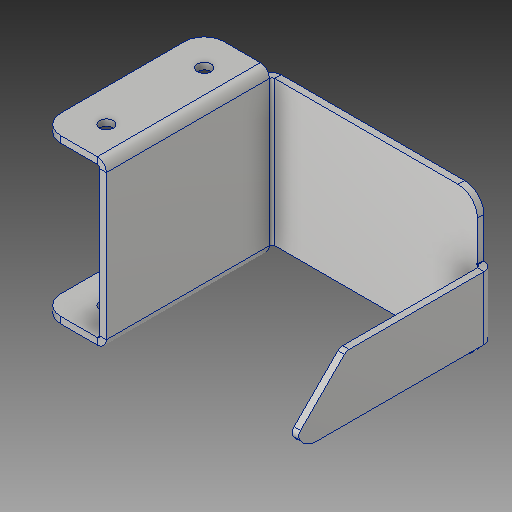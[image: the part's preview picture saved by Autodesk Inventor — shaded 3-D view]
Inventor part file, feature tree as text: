
AUTODESK INVENTOR PART (.ipt)
format: ipt  version: 2019 (Build 230136000, 136)  size: 182,784 bytes
history: native  units: mm
features: sketch x4, other x3
ambient origin geometry x8: Origin, YZ Plane, XZ Plane, XY Plane, X Axis, Y Axis, Z Axis, Center Point
bodies: Solid1 (feature_tree)
feature tree (7):
  other  "Hot End Dock.ipt"
  other  "Solid1::Hot End Dock.ipt"
  other  "TaggingFeature1"
  sketch  "Sketch1"  dims[d0=10.0mm]
  sketch  "Sketch3"
  sketch  "Sketch4"
  sketch  "Sketch5"
